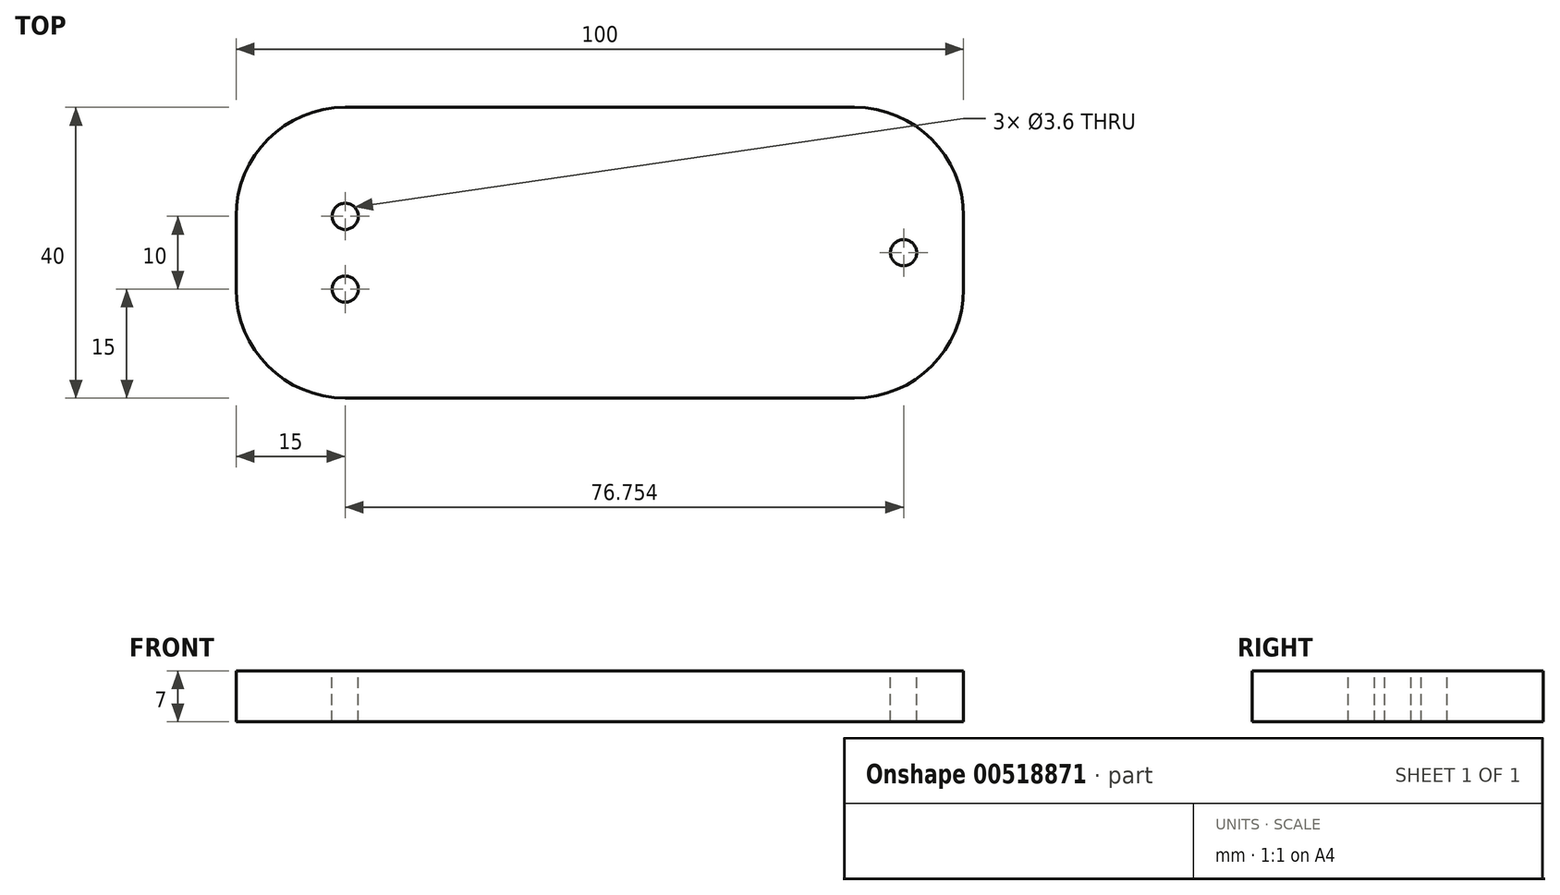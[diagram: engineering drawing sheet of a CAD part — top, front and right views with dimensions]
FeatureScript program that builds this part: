
annotation { "Feature Type Name" : "Feature", "Feature Type Description" : "" }
export const myFeature = defineFeature(function(context is Context, id is Id, definition is map)
    precondition{}
    {
        {
            var Q0;
            Q0=qCreatedBy(makeId("Top.planeOp"),FACE);
            var sketch = newSketch(context, id + "F0", { "sketchPlane" : qUnion([Q0])});
            skLineSegment(sketch, "E0.bottom", {"start": v(35, 20) * mm, "end": v(-35, 20) * mm});
            skLineSegment(sketch, "E0.top", {"start": v(35, -20) * mm, "end": v(-35, -20) * mm});
            skLineSegment(sketch, "E0.left", {"start": v(50, 5) * mm, "end": v(50, -5) * mm});
            skLineSegment(sketch, "E0.right", {"start": v(-50, 5) * mm, "end": v(-50, -5) * mm});
            skPoint(sketch, "E0.middle", {"position": v(0, 0) * mm});
            skPoint(sketch, "E1.visualSharp", {"position": v(-50, -20) * mm});
            skArc(sketch, "E1.filletArc", {"start": v(-50, -5) * mm, "mid": v(-45.6, -15.6) * mm, "end": v(-35, -20) * mm});
            skPoint(sketch, "E2.visualSharp", {"position": v(-50, 20) * mm});
            skArc(sketch, "E2.filletArc", {"start": v(-35, 20) * mm, "mid": v(-45.6, 15.6) * mm, "end": v(-50, 5) * mm});
            skPoint(sketch, "E3.visualSharp", {"position": v(50, -20) * mm});
            skArc(sketch, "E3.filletArc", {"start": v(35, -20) * mm, "mid": v(45.6, -15.6) * mm, "end": v(50, -5) * mm});
            skPoint(sketch, "E4.visualSharp", {"position": v(50, 20) * mm});
            skArc(sketch, "E4.filletArc", {"start": v(50, 5) * mm, "mid": v(45.6, 15.6) * mm, "end": v(35, 20) * mm});
            skSolve(sketch);
        }
        {
            var Q0;
            Q0 = qSketchRegion(id + "F0", true);
            extrude(context, id + "F1", {"entities" : qUnion([Q0]), "endBound" : BoundingType.SYMMETRIC, "depth" : 7 * mm, "offsetDistance" : 25 * mm});
        }
        {
            var Q0;
            Q0=makeQuery(id+"F1.opExtrude","CAP_FACE",FACE,{"disambiguationData":[OSD([sQuery(id+"F0.wireOp",EDGE,"E0.bottom"),sQuery(id+"F0.wireOp",EDGE,"E0.top"),sQuery(id+"F0.wireOp",EDGE,"E0.left"),sQuery(id+"F0.wireOp",EDGE,"E0.right"),sQuery(id+"F0.wireOp",EDGE,"E1.filletArc"),sQuery(id+"F0.wireOp",EDGE,"E2.filletArc"),sQuery(id+"F0.wireOp",EDGE,"E3.filletArc"),sQuery(id+"F0.wireOp",EDGE,"E4.filletArc")])],"isStart":false});
            var sketch = newSketch(context, id + "F2", { "sketchPlane" : qUnion([Q0])});
            skCircle(sketch, "E5", {"center": v(-35, 5) * mm, "radius": 1.8 * mm});
            skCircle(sketch, "E6", {"center": v(-35, -5) * mm, "radius": 1.8 * mm});
            skSolve(sketch);
        }
        {
            var Q0;
            Q0 = qSketchRegion(id + "F2", true);
            extrude(context, id + "F3", {"entities" : qUnion([Q0]), "operationType" : NewBodyOperationType.REMOVE, "oppositeDirection" : true, "depth" : 8 * mm, "offsetDistance" : 25 * mm});
        }
        {
            var Q0;
            Q0=makeQuery(id+"F1.opExtrude","CAP_FACE",FACE,{"disambiguationData":[OSD([sQuery(id+"F0.wireOp",EDGE,"E0.bottom"),sQuery(id+"F0.wireOp",EDGE,"E0.top"),sQuery(id+"F0.wireOp",EDGE,"E0.left"),sQuery(id+"F0.wireOp",EDGE,"E0.right"),sQuery(id+"F0.wireOp",EDGE,"E1.filletArc"),sQuery(id+"F0.wireOp",EDGE,"E2.filletArc"),sQuery(id+"F0.wireOp",EDGE,"E3.filletArc"),sQuery(id+"F0.wireOp",EDGE,"E4.filletArc")])],"isStart":false});
            var sketch = newSketch(context, id + "F4", { "sketchPlane" : qUnion([Q0])});
            skCircle(sketch, "E7", {"center": v(41.75, 0) * mm, "radius": 1.8 * mm});
            skPoint(sketch, "E8", {"position": v(50, 0) * mm});
            skSolve(sketch);
        }
        {
            var Q0;
            Q0 = qSketchRegion(id + "F4", true);
            extrude(context, id + "F5", {"entities" : qUnion([Q0]), "operationType" : NewBodyOperationType.REMOVE, "oppositeDirection" : true, "depth" : 8000 * mm, "offsetDistance" : 25 * mm});
        }
    });
